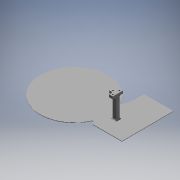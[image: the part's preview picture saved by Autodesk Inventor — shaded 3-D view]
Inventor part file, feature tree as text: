
AUTODESK INVENTOR PART (.ipt)
format: ipt  version: 2018 (Build 220112000, 112)  size: 206,848 bytes
history: native  units: mm
features: sketch x6, other x3
ambient origin geometry x8: Origin, YZ Plane, XZ Plane, XY Plane, X Axis, Y Axis, Z Axis, Center Point
bodies: Volumenkörper1 (feature_tree)
feature tree (9):
  other  "SolarpanelHalterung.ipt"
  other  "Volumenkörper1::SolarpanelHalterung.ipt"
  other  "Bezeichnung1"
  sketch  "Skizze1"  dims[d0=10.0mm]
  sketch  "Skizze2"
  sketch  "Skizze3"
  sketch  "Skizze4"
  sketch  "Skizze5"
  sketch  "Skizze6"
